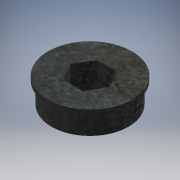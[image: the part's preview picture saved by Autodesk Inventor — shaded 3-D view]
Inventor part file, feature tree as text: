
AUTODESK INVENTOR PART (.ipt)
format: ipt  version: 2016 (Build 200138000, 138)  size: 134,144 bytes
history: native  units: in
note: dims shown in document units (in); Inventor stores cm internally (conversion verified against a paired STEP export)
features: extrude x2, sketch x2
ambient origin geometry x8: Origin, YZ Plane, XZ Plane, XY Plane, X Axis, Y Axis, Z Axis, Center Point
bodies: Solid1 (feature_tree)
feature tree (4):
  extrude  "Extrusion1"  Depth=0.5in
  extrude  "Extrusion2"  Depth=0.06in
  sketch  "Sketch1"  dims[d0=1.125in d1=0.5in]
  sketch  "Sketch2"  dims[d2=0.306in d3=0.0in d4=1.225in d5=0.06in d6=0.0in]
